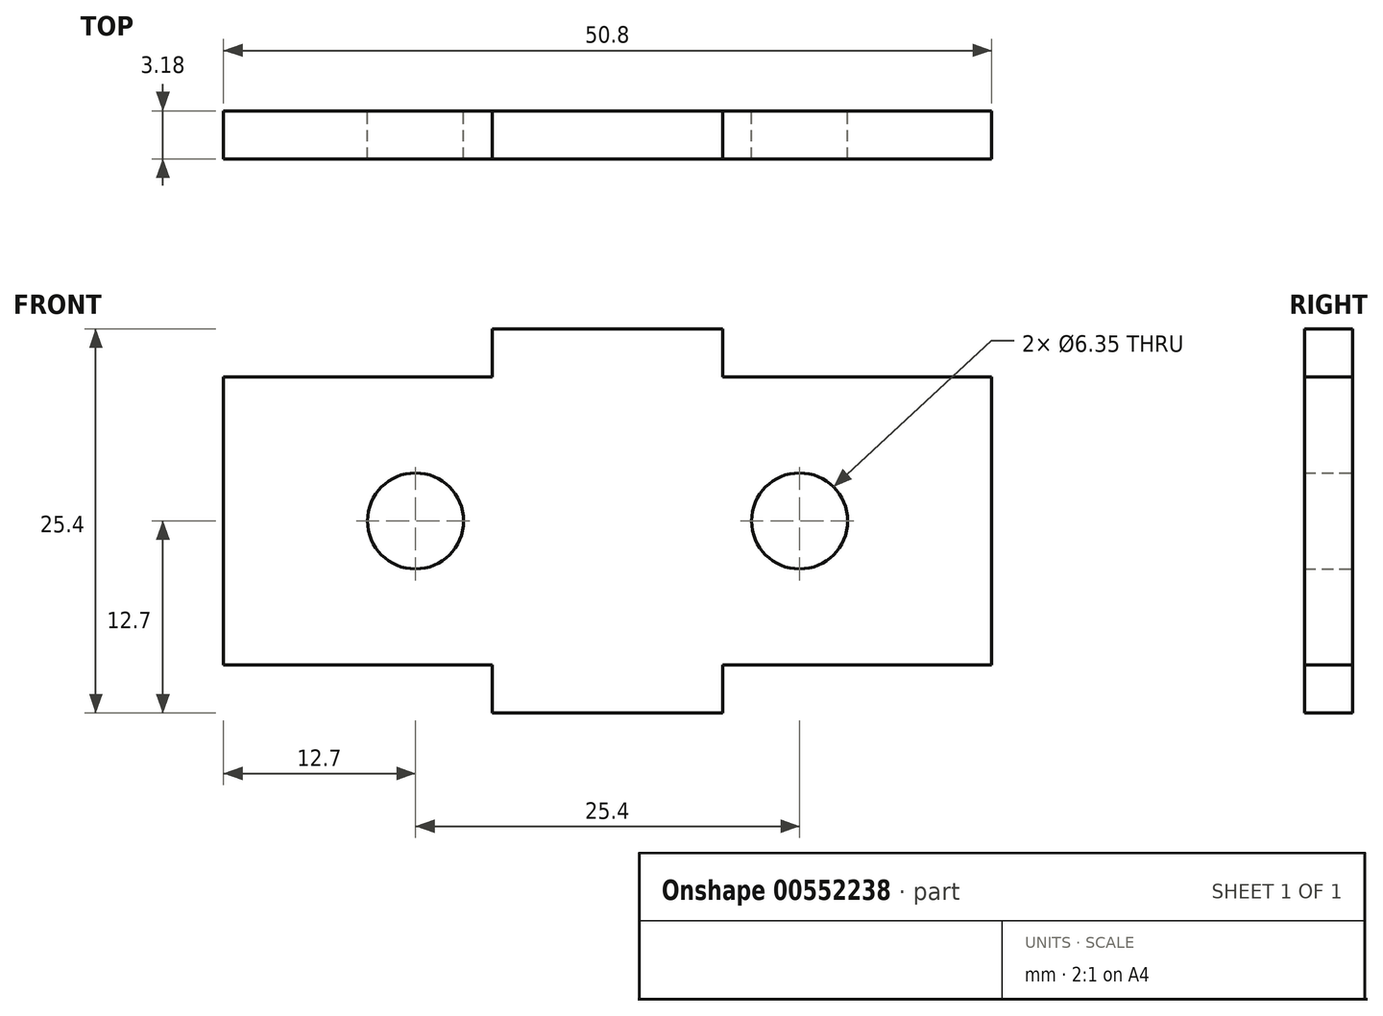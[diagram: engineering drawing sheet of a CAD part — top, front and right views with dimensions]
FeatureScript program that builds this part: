
annotation { "Feature Type Name" : "Feature", "Feature Type Description" : "" }
export const myFeature = defineFeature(function(context is Context, id is Id, definition is map)
    precondition{}
    {
        {
            var Q0;
            Q0=qCreatedBy(makeId("Front.planeOp"),FACE);
            var sketch = newSketch(context, id + "F0", { "sketchPlane" : qUnion([Q0])});
            skPoint(sketch, "E0.middle", {"position": v(0, 0) * mm});
            skCircle(sketch, "E1", {"center": v(-12.7, 0) * mm, "radius": 3.18 * mm});
            skCircle(sketch, "E2", {"center": v(12.7, 0) * mm, "radius": 3.18 * mm});
            skLineSegment(sketch, "E3", {"start": v(7.62, -12.7) * mm, "end": v(-7.62, -12.7) * mm});
            skLineSegment(sketch, "E4", {"start": v(-7.62, -12.7) * mm, "end": v(-7.62, -9.53) * mm});
            skLineSegment(sketch, "E5", {"start": v(7.62, -12.7) * mm, "end": v(7.62, -9.53) * mm});
            skLineSegment(sketch, "E6", {"start": v(25.4, 6.36) * mm, "end": v(25.4, -6.35) * mm});
            skLineSegment(sketch, "E7", {"start": v(7.62, 12.7) * mm, "end": v(-7.62, 12.7) * mm});
            skLineSegment(sketch, "E8", {"start": v(-25.4, 6.36) * mm, "end": v(-25.4, -6.35) * mm});
            skLineSegment(sketch, "E9", {"start": v(7.62, 9.53) * mm, "end": v(25.4, 9.53) * mm});
            skLineSegment(sketch, "E10", {"start": v(25.4, 9.53) * mm, "end": v(25.4, 6.36) * mm});
            skLineSegment(sketch, "E11", {"start": v(7.62, -9.53) * mm, "end": v(25.4, -9.53) * mm});
            skPoint(sketch, "E11.endSnap0", {"position": v(25.4, 7.94) * mm});
            skLineSegment(sketch, "E12", {"start": v(25.4, -9.53) * mm, "end": v(25.4, -6.35) * mm});
            skLineSegment(sketch, "E13", {"start": v(-7.62, -9.53) * mm, "end": v(-25.4, -9.53) * mm});
            skLineSegment(sketch, "E14", {"start": v(-25.4, -9.53) * mm, "end": v(-25.4, -6.35) * mm});
            skLineSegment(sketch, "E15", {"start": v(-7.62, 9.53) * mm, "end": v(-25.4, 9.53) * mm});
            skLineSegment(sketch, "E16", {"start": v(-25.4, 9.53) * mm, "end": v(-25.4, 6.36) * mm});
            skLineSegment(sketch, "E17", {"start": v(-7.62, 9.53) * mm, "end": v(-7.62, 12.7) * mm});
            skLineSegment(sketch, "E18", {"start": v(7.62, 9.53) * mm, "end": v(7.62, 12.7) * mm});
            skSolve(sketch);
        }
        {
            var Q0;
            Q0 = qSketchRegion(id + "F0", true);
            extrude(context, id + "F1", {"entities" : qUnion([Q0]), "depth" : 3.17 * mm, "offsetDistance" : 25.4 * mm});
        }
    });
